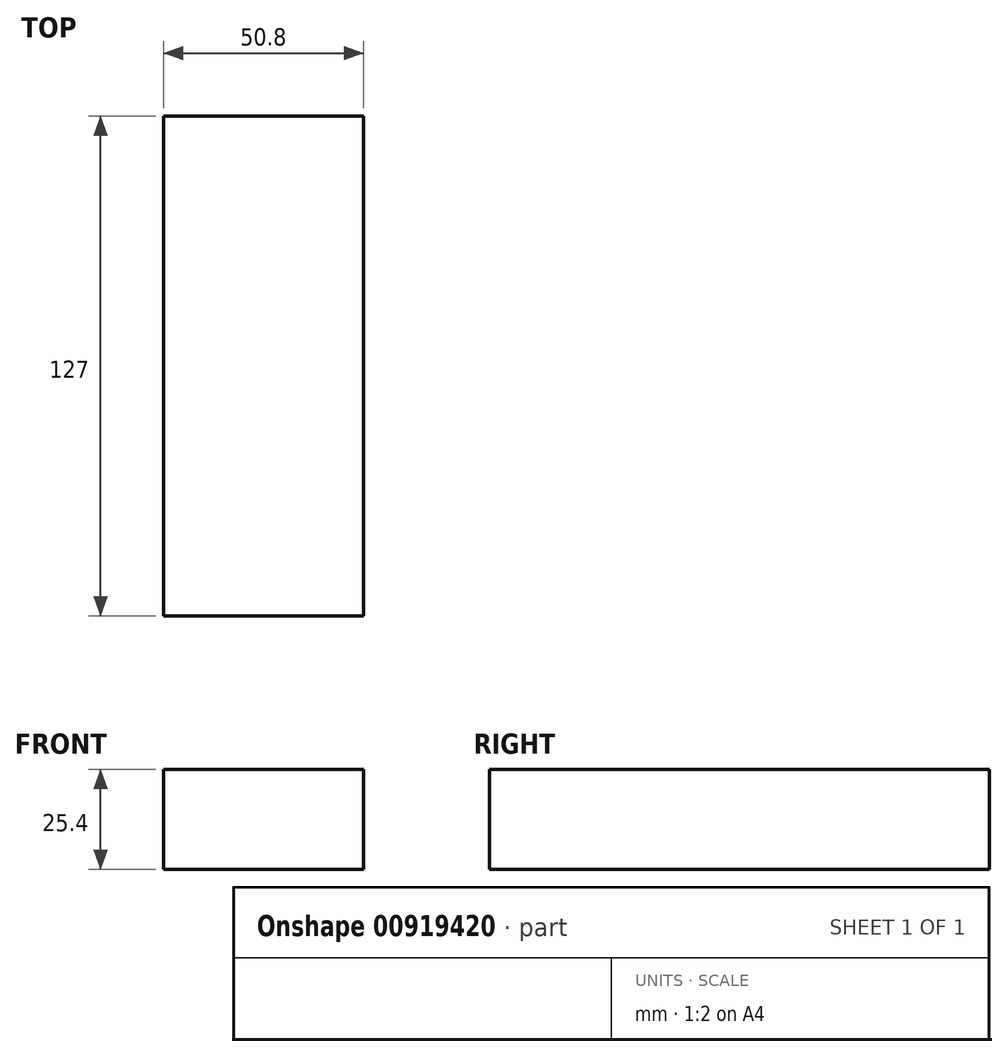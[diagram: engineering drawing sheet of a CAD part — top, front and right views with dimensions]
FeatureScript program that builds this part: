
annotation { "Feature Type Name" : "Feature", "Feature Type Description" : "" }
export const myFeature = defineFeature(function(context is Context, id is Id, definition is map)
    precondition{}
    {
        {
            var Q0;
            Q0=qCreatedBy(makeId("Top.planeOp"),FACE);
            var sketch = newSketch(context, id + "F0", { "sketchPlane" : qUnion([Q0])});
            skLineSegment(sketch, "E0.bottom", {"start": v(-24.76, 59) * mm, "end": v(26.04, 59) * mm});
            skLineSegment(sketch, "E0.top", {"start": v(-24.76, -68) * mm, "end": v(26.04, -68) * mm});
            skLineSegment(sketch, "E0.left", {"start": v(-24.76, 59) * mm, "end": v(-24.76, -68) * mm});
            skLineSegment(sketch, "E0.right", {"start": v(26.04, 59) * mm, "end": v(26.04, -68) * mm});
            skSolve(sketch);
        }
        {
            var Q0;
            Q0 = qSketchRegion(id + "F0", true);
            var sketch = newSketch(context, id + "F1", { "sketchPlane" : qUnion([Q0])});
            skSolve(sketch);
        }
        {
            var Q0;
            Q0=makeQuery(id+"F1.imprint","IMPRINT",FACE,{"disambiguationData":[TD([[makeQuery(id+"F1.imprint","IMPRINT",EDGE,{"derivedFrom":makeQuery(id+"F0.imprint","IMPRINT",EDGE,{"derivedFrom":sQuery(id+"F0.wireOp",EDGE,"E0.bottom")})}),-1.0]])]});
            extrude(context, id + "F2", {"entities" : qUnion([Q0]), "depth" : 25.4 * mm, "offsetDistance" : 25.4 * mm});
        }
    });
